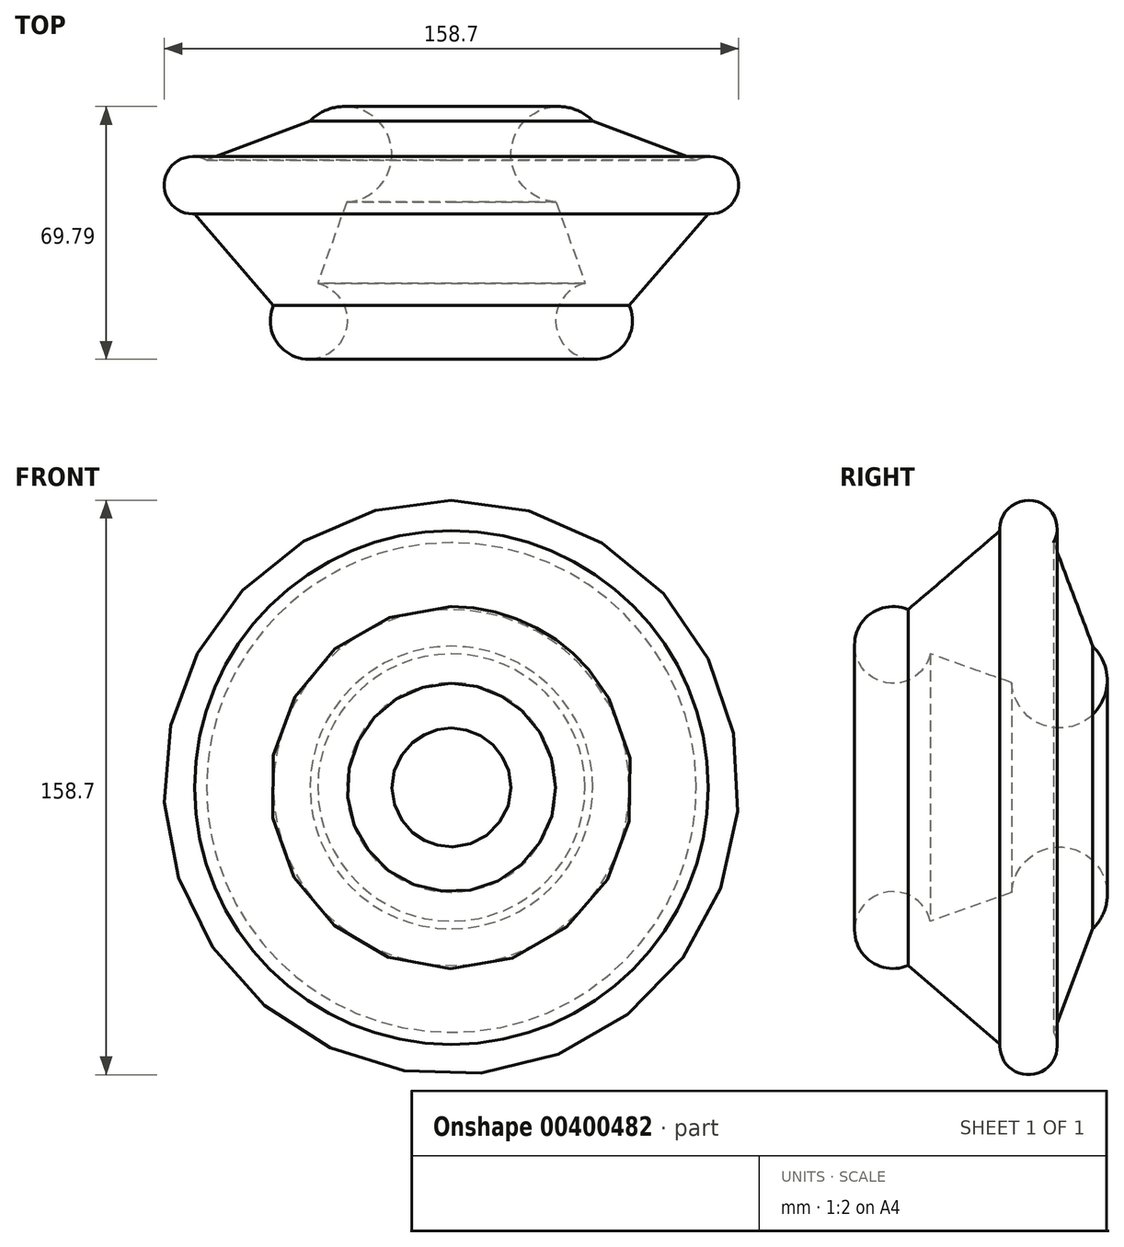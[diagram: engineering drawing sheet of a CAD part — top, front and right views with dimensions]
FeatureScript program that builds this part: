
annotation { "Feature Type Name" : "Feature", "Feature Type Description" : "" }
export const myFeature = defineFeature(function(context is Context, id is Id, definition is map)
    precondition{}
    {
        {
            var Q0;
            Q0=qCreatedBy(makeId("Top.planeOp"),FACE);
            var sketch = newSketch(context, id + "F0", { "sketchPlane" : qUnion([Q0])});
            skCircle(sketch, "E0", {"center": v(-46.98, 42.82) * mm, "radius": 7.9 * mm});
            skCircle(sketch, "E1", {"center": v(-5.13, 51.38) * mm, "radius": 13.18 * mm});
            skCircle(sketch, "E2", {"center": v(-14.93, 5.38) * mm, "radius": 10.61 * mm});
            skLineSegment(sketch, "E3", {"start": v(-10.94, 39.55) * mm, "end": v(-21.5, 13.72) * mm});
            skLineSegment(sketch, "E4", {"start": v(-4.47, 38.22) * mm, "end": v(-12.45, 15.7) * mm});
            skLineSegment(sketch, "E5", {"start": v(-41.57, 37.05) * mm, "end": v(-21.5, 13.72) * mm});
            skLineSegment(sketch, "E6", {"start": v(-46.49, 34.93) * mm, "end": v(-24.68, 9.57) * mm});
            skLineSegment(sketch, "E7", {"start": v(-43.17, 49.75) * mm, "end": v(-14.57, 60.58) * mm});
            skLineSegment(sketch, "E8", {"start": v(-39.17, 44.04) * mm, "end": v(-18.24, 50.08) * mm});
            skLineSegment(sketch, "E9", {"start": v(24.47, 62.4) * mm, "end": v(24.47, -3.67) * mm});
            skSolve(sketch);
        }
        {
            var Q0;
            {var subQ0=sQuery(id+"F0.wireOp",EDGE,"E3");Q0=makeQuery(id+"F0.imprint","IMPRINT",FACE,{"disambiguationData":[TD([[makeQuery(id+"F0.imprint","IMPRINT",EDGE,{"derivedFrom":subQ0}),-1.0]])]});}
            var Q1;
            {var subQ0=sQuery(id+"F0.wireOp",EDGE,"E3");Q1=makeQuery(id+"F0.imprint","IMPRINT",FACE,{"disambiguationData":[TD([[makeQuery(id+"F0.imprint","IMPRINT",EDGE,{"derivedFrom":subQ0}),1.0]])]});}
            var Q2;
            {var subQ0=sQuery(id+"F0.wireOp",EDGE,"E7");Q2=makeQuery(id+"F0.imprint","IMPRINT",FACE,{"disambiguationData":[TD([[makeQuery(id+"F0.imprint","IMPRINT",EDGE,{"derivedFrom":subQ0}),-1.0]])]});}
            var Q3;
            {var subQ0=sQuery(id+"F0.wireOp",EDGE,"E2");var subQ2=makeQuery(id+"F0.imprint","INTERSECT",VERTEX,{"derivedFrom":[subQ0,sQuery(id+"F0.wireOp",EDGE,"E4")]});Q3=makeQuery(id+"F0.imprint","IMPRINT",FACE,{"disambiguationData":[TD([[makeQuery(id+"F0.imprint","IMPRINT",EDGE,{"disambiguationData":[TD([[subQ2,1.0]])],"derivedFrom":subQ0}),1.0]])]});}
            var Q4;
            {var subQ0=sQuery(id+"F0.wireOp",EDGE,"E1");var subQ1=makeQuery(id+"F0.imprint","INTERSECT",VERTEX,{"derivedFrom":[subQ0,sQuery(id+"F0.wireOp",EDGE,"E7")]});Q4=makeQuery(id+"F0.imprint","IMPRINT",FACE,{"disambiguationData":[TD([[makeQuery(id+"F0.imprint","IMPRINT",EDGE,{"disambiguationData":[TD([[subQ1,-1.0]])],"derivedFrom":subQ0}),1.0]])]});}
            var Q5;
            {var subQ0=sQuery(id+"F0.wireOp",EDGE,"E0");var subQ1=makeQuery(id+"F0.imprint","INTERSECT",VERTEX,{"derivedFrom":[subQ0,sQuery(id+"F0.wireOp",EDGE,"E7")]});Q5=makeQuery(id+"F0.imprint","IMPRINT",FACE,{"disambiguationData":[TD([[makeQuery(id+"F0.imprint","IMPRINT",EDGE,{"disambiguationData":[TD([[subQ1,1.0]])],"derivedFrom":subQ0}),1.0]])]});}
            var Q6;
            {var subQ0=sQuery(id+"F0.wireOp",EDGE,"E5");Q6=makeQuery(id+"F0.imprint","IMPRINT",FACE,{"disambiguationData":[TD([[makeQuery(id+"F0.imprint","IMPRINT",EDGE,{"derivedFrom":subQ0}),-1.0]])]});}
            var Q7;
            Q7=sQuery(id+"F0.wireOp",EDGE,"E9");
            revolve(context, id + "F1", {"entities" : qUnion([Q0, Q1, Q2, Q3, Q4, Q5, Q6]), "axis" : qUnion([Q7]), "revolveType" : RevolveType.FULL});
        }
    });
